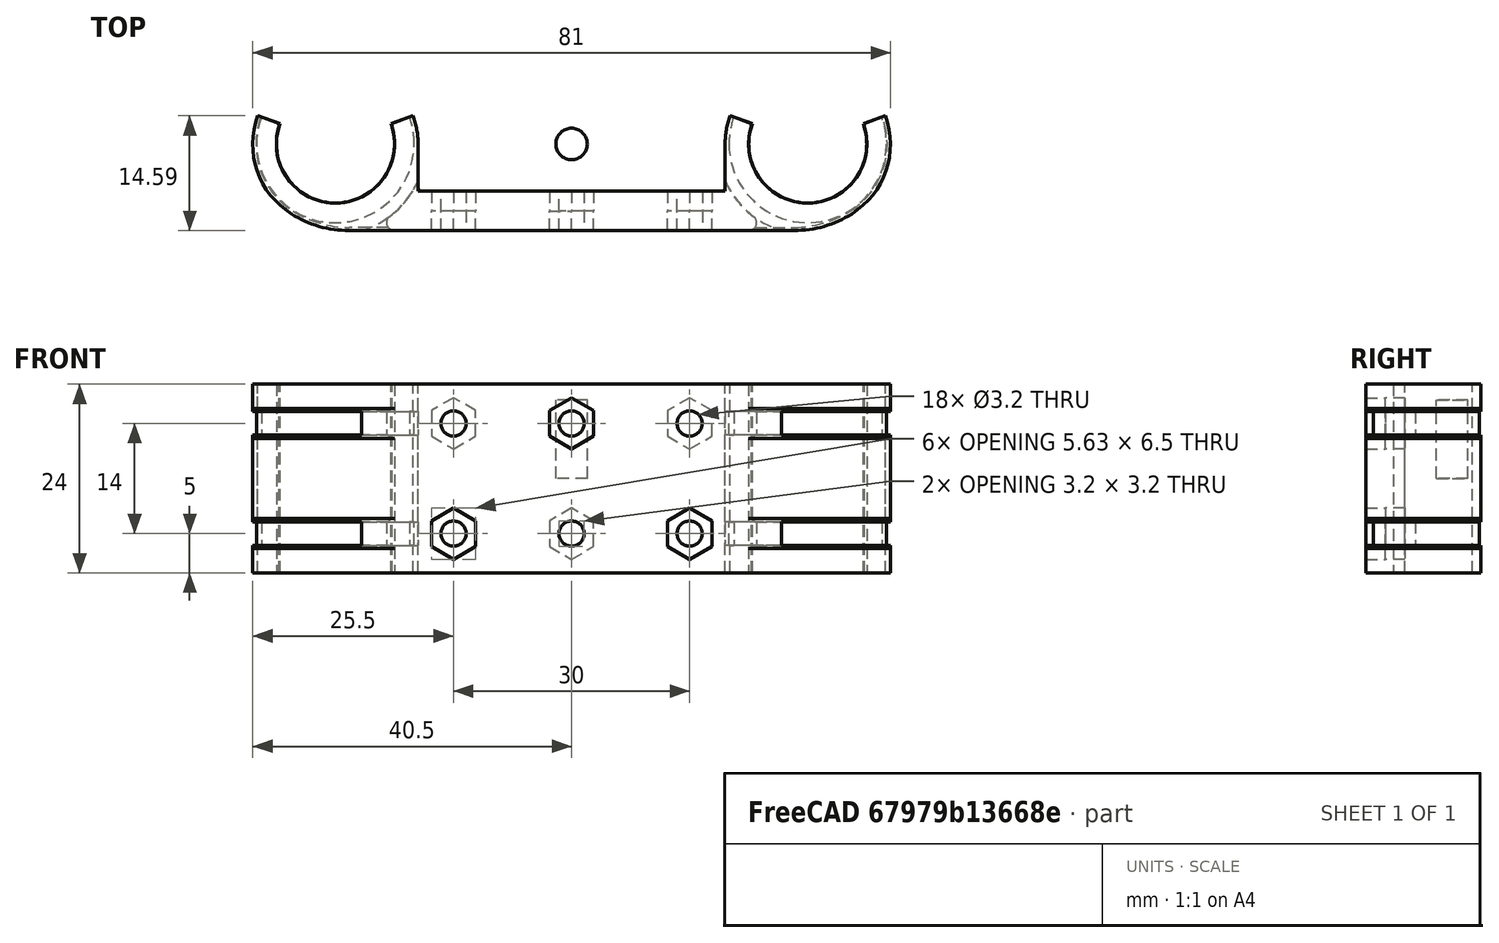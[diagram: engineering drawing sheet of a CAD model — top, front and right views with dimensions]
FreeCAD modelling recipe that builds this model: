
FCSTD DOCUMENT  (FreeCAD 0.16R6712 (Git))
Label: universal_carriage_v1a
License: All rights reserved
LicenseURL: http://en.wikipedia.org/wiki/All_rights_reserved
objects: Spreadsheet::Sheet×5, Mesh::Feature×4, Sketcher::SketchObject×4, PartDesign::Pad×4, Part::FeaturePython×3, Part::MultiFuse×3, Part::Cut×2, Part::Feature×2, PartDesign::Fillet×2, Part::Cylinder×1, App::DocumentObjectGroup×1, Part::Mirroring×1, PartDesign::Chamfer×1
note: 27 computed .brp shape members not serialized (recipe doc carries the construction recipe); baked Part::Feature solids carry a one-line shape summary decoded from their .brp

FEATURE [Mesh::Feature] carriage
FEATURE [Part::Cylinder] Cylinder
  Angle = 360
  Height = 10
  Radius = 2
FEATURE [Mesh::Feature] idler_end_v3
FEATURE [Mesh::Feature] carriage001  label="carriage"
FEATURE [Mesh::Feature] MagCarriage
  Placement = pos=(40,-4,-12) rot=(0.57735,-0.57735,-0.57735;2.0944rad)
FEATURE [Sketcher::SketchObject] Sketch
  sketch-geometry (12):
    g0: ArcOfCircle CenterX=-30 CenterY=0 CenterZ=0 NormalX=0 NormalY=0 NormalZ=1 Radius=7.5 StartAngle=2.79253 EndAngle=6.63225
    g1: ArcOfCircle CenterX=-30 CenterY=0 CenterZ=0 NormalX=0 NormalY=0 NormalZ=1 Radius=10.5 StartAngle=2.79253 EndAngle=4.15082
    g2: LineSegment StartX=-37.0477 StartY=2.56515 StartZ=0 EndX=-39.8668 EndY=3.59121 EndZ=0
    g3: LineSegment StartX=-22.9523 StartY=2.56515 StartZ=0 EndX=-20.1332 EndY=3.59121 EndZ=0
    g4: LineSegment StartX=-19.5 StartY=-6 StartZ=0 EndX=0 EndY=-6 EndZ=0
    g5: LineSegment StartX=0 StartY=-6 StartZ=0 EndX=0 EndY=-11 EndZ=0
    g6: LineSegment [constr] StartX=-37.0477 StartY=2.56515 StartZ=0 EndX=-30 EndY=0 EndZ=0
    g7: LineSegment [constr] StartX=-30 StartY=0 StartZ=0 EndX=-22.9523 EndY=2.56515 EndZ=0
    g8: ArcOfCircle CenterX=-30 CenterY=0 CenterZ=0 NormalX=0 NormalY=0 NormalZ=1 Radius=10.5 StartAngle=0 EndAngle=0.349066
    g9: LineSegment StartX=-19.5 StartY=0 StartZ=0 EndX=-19.5 EndY=-6 EndZ=0
    g10: LineSegment StartX=0 StartY=-11 StartZ=0 EndX=-28.2663 EndY=-11 EndZ=0
    g11: ArcOfCircle CenterX=-28.2663 CenterY=2.75573 CenterZ=0 NormalX=0 NormalY=0 NormalZ=1 Radius=13.7557 StartAngle=4.15082 EndAngle=4.71239
  constraints (35):
    c: PointOnObject(g0,g-1)
    c: DistanceX(g0,g-1) = 30
    c: Coincident(g1,g0)
    c: Radius(g0) = 7.5
    c: Coincident(g2,g0)
    c: Coincident(g1,g2)
    c: Perpendicular(g1,g2)
    c: Coincident(g0,g3)
    c: Horizontal(g4)
    c: Coincident(g4,g5)
    c: Vertical(g5)
    c: Equal(g3,g2)
    c: Coincident(g6,g0)
    c: Coincident(g6,g0)
    c: Angle(g-1,g6) = 2.79253
    c: Coincident(g7,g0)
    c: Coincident(g7,g0)
    c: Angle(g7,g-1) = 2.79253
    c: Coincident(g8,g0)
    c: Coincident(g8,g3)
    c: PointOnObject(g8,g-1)
    c: Coincident(g9,g8)
    c: Coincident(g9,g4)
    c: Vertical(g9)
    c: DistanceY(g4,g-1) = 6
    c: Perpendicular(g0,g3)
    c: Coincident(g5,g10)
    c: Horizontal(g10)
    c: PointOnObject(g4,g-2)
    c: DistanceY(g5,g5) = 5
    c: Coincident(g11,g10)
    c: Coincident(g11,g1)
    c: Tangent(g11,g10)
    c: Tangent(g11,g1)
    c: Distance(g2) = 3
FEATURE [PartDesign::Pad] Pad
  Length = 24
  Length2 = 100
  Midplane = true
  Sketch = -> Sketch
  Type = 0
FEATURE [Spreadsheet::Sheet] Spreadsheet007  label="Screw_M3"
  cells = A1=Name; B1=Value; C1=Description; A2=Designation; B2=M3x10; A3=T; B3(T)==0.1mm + Printer.T; C3=Screw dimension tolerance (including printer T); A4=ideal_r; B4(ideal_r)==1.5mm; C4=Ideal screw thread radius; A5=thread_r; B5(thread_r)==ideal_r + T; C5=Pass through hole radius; A6=thread_length; B6(thread_length)==10mm; C6=Screw thread length; A7=head_r; B7(head_r)==5.7mm / 2 + T; C7=Screw head radius; A8=head_length; B8(head_length)==3mm; C8=Screw head length (height); A9=head_clearance; B9(head_clearance)==10mm; C9=Needed clearance above screw head; A10=head_slope_length; B10(head_slope_length)==ceil((head_r - thread_r) / Printer.default_layer) * Printer.default_layer; C10=45deg slop to make it easier to print; A11=arm_r; B11(arm_r)==head_r + Printer.wall_4d; C11=Holder arm going around head; A12=arm_min_r; B12(arm_min_r)==thread_r + Printer.wall_2d; C12=Holder arm going around thread only; A13=arm_thickness; B13(arm_thickness)==5mm; C13=Suggested arm thickness; A14=cut_r; B14(cut_r)==ideal_r - 0.05mm; C14=Planar threaded hole cut radius; A15=vcut_r; B15(vcut_r)==floor(cut_r / Printer.default_layer) * Printer.default_layer; C15=Vertical threaded hole cut radius
FEATURE [Spreadsheet::Sheet] Spreadsheet005  label="Screw_M6"
  cells = A1=Name; B1=Value; C1=Description; A2=Designation; B2=M6x25; A3=T; B3(T)==0.1mm + Printer.T; C3=Screw dimension tolerance (including printer T); A4=ideal_r; B4(ideal_r)==3mm; C4=Ideal screw thread radius; A5=thread_r; B5(thread_r)==3mm + T; C5=Pass through hole radius; A6=thread_length; B6(thread_length)==25mm; C6=Screw thread length; A7=head_r; B7(head_r)==5mm + T; C7=Screw head radius; A8=head_length; B8(head_length)==4mm; C8=Screw head length (height); A9=arm_r; B9(arm_r)==head_r + Printer.wall_4d; C9=Holder arm going around head; A10=arm_min_r; B10(arm_min_r)==thread_r + Printer.wall_2d; C10=Holder arm going around thread only; A11=arm_thickness; B11(arm_thickness)==7mm; C11=Suggested arm thickness; A12=cut_r; B12(cut_r)==2.9mm; C12=Planar threaded hole cut radius; A13=vcut_r; B13(vcut_r)==floor(cut_r / Printer.default_layer) * Printer.default_layer; C13=Vertical threaded hole cut radius
FEATURE [Spreadsheet::Sheet] Spreadsheet006  label="Nut_M6"
  cells = A1=Name; B1=Value; C1=Description; A2=T; B2(T)==0mm + Printer.T; C2=Dimension tolerance (including printer T); A3=outer_r; B3(outer_r)==11.2mm / 2; C3=Outer most nut radius; A4=width; B4(width)==10mm; C4=Nut side width; A5=thickness; B5(thickness)==5mm; C5=Nut thickness (height); A6=num_of_sides; B6(num_of_sides)=6; C6=Number of sides
FEATURE [Spreadsheet::Sheet] Spreadsheet008  label="Nut_M3"
  cells = A1=Name; B1=Value; C1=Description; A2=T; B2(T)==0mm + Printer.T; C2=Dimension tolerance (including printer T); A3=outer_r; B3(outer_r)==6.5mm / 2 + T; C3=Outer most nut radius; A4=width; B4(width)==5.5mm + T; C4=Nut side width; A5=thickness; B5(thickness)==2.5mm; C5=Nut thickness (height); A6=num_of_sides; B6(num_of_sides)=6; C6=Number of sides
FEATURE [Sketcher::SketchObject] Sketch001
  Placement = pos=(0,-6,0) rot=(1,0,0;1.5708rad)
  expr: Constraints[38] = Nut_M3.outer_r
  sketch-geometry (24):
    g0: LineSegment StartX=-12.1854 StartY=5.375 StartZ=0 EndX=-12.1854 EndY=8.625 EndZ=0
    g1: LineSegment StartX=-12.1854 StartY=8.625 StartZ=0 EndX=-15 EndY=10.25 EndZ=0
    g2: LineSegment StartX=-15 StartY=10.25 StartZ=0 EndX=-17.8146 EndY=8.625 EndZ=0
    g3: LineSegment StartX=-17.8146 StartY=8.625 StartZ=0 EndX=-17.8146 EndY=5.375 EndZ=0
    g4: LineSegment StartX=-17.8146 StartY=5.375 StartZ=0 EndX=-15 EndY=3.75 EndZ=0
    g5: LineSegment StartX=-15 StartY=3.75 StartZ=0 EndX=-12.1854 EndY=5.375 EndZ=0
    g6: Circle [constr] CenterX=-15 CenterY=7 CenterZ=0 NormalX=0 NormalY=0 NormalZ=1 Radius=3.25
    g7: LineSegment StartX=2.81458 StartY=-8.625 StartZ=0 EndX=2.81458 EndY=-5.375 EndZ=0
    g8: LineSegment StartX=2.81458 StartY=-5.375 StartZ=0 EndX=0 EndY=-3.75 EndZ=0
    g9: LineSegment StartX=0 StartY=-3.75 StartZ=0 EndX=-2.81458 EndY=-5.375 EndZ=0
    g10: LineSegment StartX=-2.81458 StartY=-5.375 StartZ=0 EndX=-2.81458 EndY=-8.625 EndZ=0
    g11: LineSegment StartX=-2.81458 StartY=-8.625 StartZ=0 EndX=0 EndY=-10.25 EndZ=0
    g12: LineSegment StartX=0 StartY=-10.25 StartZ=0 EndX=2.81458 EndY=-8.625 EndZ=0
    g13: Circle [constr] CenterX=0 CenterY=-7 CenterZ=0 NormalX=0 NormalY=0 NormalZ=1 Radius=3.25
    g14: LineSegment [constr] StartX=0 StartY=-7 StartZ=0 EndX=0 EndY=0 EndZ=0
    g15: LineSegment [constr] StartX=-15 StartY=7 StartZ=0 EndX=-15 EndY=0 EndZ=0
    g16: LineSegment StartX=17.8146 StartY=5.375 StartZ=0 EndX=17.8146 EndY=8.625 EndZ=0
    g17: LineSegment StartX=17.8146 StartY=8.625 StartZ=0 EndX=15 EndY=10.25 EndZ=0
    g18: LineSegment StartX=15 StartY=10.25 StartZ=0 EndX=12.1854 EndY=8.625 EndZ=0
    g19: LineSegment StartX=12.1854 StartY=8.625 StartZ=0 EndX=12.1854 EndY=5.375 EndZ=0
    g20: LineSegment StartX=12.1854 StartY=5.375 StartZ=0 EndX=15 EndY=3.75 EndZ=0
    g21: LineSegment StartX=15 StartY=3.75 StartZ=0 EndX=17.8146 EndY=5.375 EndZ=0
    g22: Circle [constr] CenterX=15 CenterY=7 CenterZ=0 NormalX=0 NormalY=0 NormalZ=1 Radius=3.25
    g23: LineSegment [constr] StartX=-15 StartY=7 StartZ=0 EndX=15 EndY=7 EndZ=0
  constraints (58):
    c: Coincident(g0,g1)
    c: Coincident(g1,g2)
    c: Coincident(g2,g3)
    c: Coincident(g3,g4)
    c: Coincident(g4,g5)
    c: Coincident(g5,g0)
    c: Equal(g0, g1-g5) x5
    c: PointOnObject(g0,g6)
    c: PointOnObject(g1,g6)
    c: PointOnObject(g2,g6)
    c: PointOnObject(g3,g6)
    c: PointOnObject(g4,g6)
    c: PointOnObject(g5,g6)
    c: Coincident(g7,g8)
    c: Coincident(g8,g9)
    c: Coincident(g9,g10)
    c: Coincident(g10,g11)
    c: Coincident(g11,g12)
    c: Coincident(g12,g7)
    c: Equal(g7, g8-g12) x5
    c: PointOnObject(g7,g13)
    c: PointOnObject(g8,g13)
    c: PointOnObject(g9,g13)
    c: PointOnObject(g10,g13)
    c: PointOnObject(g11,g13)
    c: PointOnObject(g12,g13)
    c: PointOnObject(g13,g-2)
    c: Vertical(g3)
    c: Vertical(g10)
    c: Equal(g6,g13)
    c: Radius(g6) = 3.25
    c: Coincident(g14,g13)
    c: Coincident(g14,g-1)
    c: Coincident(g15,g6)
    c: Vertical(g15)
    c: Equal(g15,g14)
    c: PointOnObject(g15,g-1)
    c: DistanceY(g14,g14) = 7
    c: DistanceX(g15,g-1) = 15
    c: Coincident(g16,g17)
    c: Coincident(g17,g18)
    c: Coincident(g18,g19)
    c: Coincident(g19,g20)
    c: Coincident(g20,g21)
    c: Coincident(g21,g16)
    c: Equal(g16, g17-g21) x5
    c: PointOnObject(g16,g22)
    c: PointOnObject(g17,g22)
    c: PointOnObject(g18,g22)
    c: PointOnObject(g19,g22)
    c: PointOnObject(g20,g22)
    c: PointOnObject(g21,g22)
    c: Coincident(g23,g6)
    c: Coincident(g23,g22)
    c: Horizontal(g23)
    c: Vertical(g19)
    c: Equal(g22,g6)
    c: Symmetric(g22,g6,g-2)
FEATURE [Spreadsheet::Sheet] Spreadsheet011  label="Printer"
  cells = A1=Name; B1=Value; C1=Description; A2=printer; B2=Prusa i3 MK2; C2=Printer name; A3=T; B3(T)==0mm; C3=Dimensional deviation of XY axis; A4=T_v; B4(T_v)==0mm; C4=Dimensional deviation of Z axis; A5=T_max; B5(T_max)==0.4mm; C5=Maximal expected deviation; A6=nozzle_d; B6(nozzle_d)==0.4mm; C6=Nozzle diameter; A7=thinnes_wall; B7(thinnest_wall)==2 * nozzle_d; C7=Thinnest printable wall; A8=wall_2d; B8(wall_2d)==2 * nozzle_d; C8=2D wall without infill; A9=wall_3d; B9(wall_3d)==3 * nozzle_d; C9=3D wall without infill; A10=wall_4d; B10(wall_4d)==4 * nozzle_d; C10=4D wall without infill; A11=wall_5d; B11(wall_5d)==5 * nozzle_d; C11=5D wall without infill; A12=default_layer; B12(default_layer)==0.2mm; C12=Default printing layer height
FEATURE [App::DocumentObjectGroup] Group  label="Documents"
  Group = -> [Spreadsheet007,Spreadsheet005,Spreadsheet006,Spreadsheet008,Spreadsheet011]
FEATURE [PartDesign::Pad] Pad001
  Length = 2.5
  Length2 = 100
  Placement = pos=(0,-6,0) rot=(1,0,0;1.5708rad)
  Sketch = -> Sketch001
  Type = 0
FEATURE [Sketcher::SketchObject] Sketch002
  Placement = pos=(0,-6,0) rot=(1,0,0;1.5708rad)
  expr: Constraints[82] = 1.6mm
  expr: Constraints[38] = Nut_M3.outer_r
  sketch-geometry (30):
    g0: LineSegment [constr] StartX=-12.1854 StartY=5.375 StartZ=0 EndX=-12.1854 EndY=8.625 EndZ=0
    g1: LineSegment [constr] StartX=-12.1854 StartY=8.625 StartZ=0 EndX=-15 EndY=10.25 EndZ=0
    g2: LineSegment [constr] StartX=-15 StartY=10.25 StartZ=0 EndX=-17.8146 EndY=8.625 EndZ=0
    g3: LineSegment [constr] StartX=-17.8146 StartY=8.625 StartZ=0 EndX=-17.8146 EndY=5.375 EndZ=0
    g4: LineSegment [constr] StartX=-17.8146 StartY=5.375 StartZ=0 EndX=-15 EndY=3.75 EndZ=0
    g5: LineSegment [constr] StartX=-15 StartY=3.75 StartZ=0 EndX=-12.1854 EndY=5.375 EndZ=0
    g6: Circle [constr] CenterX=-15 CenterY=7 CenterZ=0 NormalX=0 NormalY=0 NormalZ=1 Radius=3.25
    g7: LineSegment [constr] StartX=2.81458 StartY=-8.625 StartZ=0 EndX=2.81458 EndY=-5.375 EndZ=0
    g8: LineSegment [constr] StartX=2.81458 StartY=-5.375 StartZ=0 EndX=0 EndY=-3.75 EndZ=0
    g9: LineSegment [constr] StartX=0 StartY=-3.75 StartZ=0 EndX=-2.81458 EndY=-5.375 EndZ=0
    g10: LineSegment [constr] StartX=-2.81458 StartY=-5.375 StartZ=0 EndX=-2.81458 EndY=-8.625 EndZ=0
    g11: LineSegment [constr] StartX=-2.81458 StartY=-8.625 StartZ=0 EndX=0 EndY=-10.25 EndZ=0
    g12: LineSegment [constr] StartX=0 StartY=-10.25 StartZ=0 EndX=2.81458 EndY=-8.625 EndZ=0
    g13: Circle [constr] CenterX=0 CenterY=-7 CenterZ=0 NormalX=0 NormalY=0 NormalZ=1 Radius=3.25
    g14: LineSegment [constr] StartX=0 StartY=-7 StartZ=0 EndX=0 EndY=0 EndZ=0
    g15: LineSegment [constr] StartX=-15 StartY=7 StartZ=0 EndX=-15 EndY=0 EndZ=0
    g16: LineSegment [constr] StartX=17.8146 StartY=5.375 StartZ=0 EndX=17.8146 EndY=8.625 EndZ=0
    g17: LineSegment [constr] StartX=17.8146 StartY=8.625 StartZ=0 EndX=15 EndY=10.25 EndZ=0
    g18: LineSegment [constr] StartX=15 StartY=10.25 StartZ=0 EndX=12.1854 EndY=8.625 EndZ=0
    g19: LineSegment [constr] StartX=12.1854 StartY=8.625 StartZ=0 EndX=12.1854 EndY=5.375 EndZ=0
    g20: LineSegment [constr] StartX=12.1854 StartY=5.375 StartZ=0 EndX=15 EndY=3.75 EndZ=0
    g21: LineSegment [constr] StartX=15 StartY=3.75 StartZ=0 EndX=17.8146 EndY=5.375 EndZ=0
    g22: Circle [constr] CenterX=15 CenterY=7 CenterZ=0 NormalX=0 NormalY=0 NormalZ=1 Radius=3.25
    g23: LineSegment [constr] StartX=-15 StartY=7 StartZ=0 EndX=15 EndY=7 EndZ=0
    g24: Circle CenterX=-15 CenterY=7 CenterZ=0 NormalX=0 NormalY=0 NormalZ=1 Radius=1.6
    g25: Circle CenterX=0 CenterY=-7 CenterZ=0 NormalX=0 NormalY=0 NormalZ=1 Radius=1.6
    g26: Circle CenterX=15 CenterY=7 CenterZ=0 NormalX=0 NormalY=0 NormalZ=1 Radius=1.6
    g27: Circle CenterX=-15 CenterY=-7 CenterZ=0 NormalX=0 NormalY=0 NormalZ=1 Radius=1.6
    g28: Circle CenterX=0 CenterY=7 CenterZ=0 NormalX=0 NormalY=0 NormalZ=1 Radius=1.6
    g29: Circle CenterX=15 CenterY=-7 CenterZ=0 NormalX=0 NormalY=0 NormalZ=1 Radius=1.6
  constraints (71):
    c: Coincident(g0,g1)
    c: Coincident(g1,g2)
    c: Coincident(g2,g3)
    c: Coincident(g3,g4)
    c: Coincident(g4,g5)
    c: Coincident(g5,g0)
    c: Equal(g0, g1-g5) x5
    c: PointOnObject(g0,g6)
    c: PointOnObject(g1,g6)
    c: PointOnObject(g2,g6)
    c: PointOnObject(g3,g6)
    c: PointOnObject(g4,g6)
    c: PointOnObject(g5,g6)
    c: Coincident(g7,g8)
    c: Coincident(g8,g9)
    c: Coincident(g9,g10)
    c: Coincident(g10,g11)
    c: Coincident(g11,g12)
    c: Coincident(g12,g7)
    c: Equal(g7, g8-g12) x5
    c: PointOnObject(g7,g13)
    c: PointOnObject(g8,g13)
    c: PointOnObject(g9,g13)
    c: PointOnObject(g10,g13)
    c: PointOnObject(g11,g13)
    c: PointOnObject(g12,g13)
    c: PointOnObject(g13,g-2)
    c: Vertical(g3)
    c: Vertical(g10)
    c: Equal(g6,g13)
    c: Radius(g6) = 3.25
    c: Coincident(g14,g13)
    c: Coincident(g14,g-1)
    c: Coincident(g15,g6)
    c: Vertical(g15)
    c: Equal(g15,g14)
    c: PointOnObject(g15,g-1)
    c: DistanceY(g14,g14) = 7
    c: DistanceX(g15,g-1) = 15
    c: Coincident(g16,g17)
    c: Coincident(g17,g18)
    c: Coincident(g18,g19)
    c: Coincident(g19,g20)
    c: Coincident(g20,g21)
    c: Coincident(g21,g16)
    c: Equal(g16, g17-g21) x5
    c: PointOnObject(g16,g22)
    c: PointOnObject(g17,g22)
    c: PointOnObject(g18,g22)
    c: PointOnObject(g19,g22)
    c: PointOnObject(g20,g22)
    c: PointOnObject(g21,g22)
    c: Coincident(g23,g6)
    c: Coincident(g23,g22)
    c: Horizontal(g23)
    c: Vertical(g19)
    c: Equal(g22,g6)
    c: Symmetric(g22,g6,g-2)
    c: Coincident(g24,g6)
    c: Coincident(g25,g13)
    c: Coincident(g26,g22)
    c: PointOnObject(g28,g23)
    c: Symmetric(g6,g27,g-1)
    c: Symmetric(g28,g13,g-1)
    c: Symmetric(g22,g29,g-1)
    c: Equal(g29,g25)
    c: Equal(g25,g27)
    c: Equal(g27,g24)
    c: Equal(g24,g28)
    c: Equal(g28,g26)
    c: Radius(g27) = 1.6
FEATURE [PartDesign::Pad] Pad002
  Length = 10
  Length2 = 100
  Placement = pos=(0,-6,0) rot=(1,0,0;1.5708rad)
  Sketch = -> Sketch002
  Type = 0
FEATURE [Part::FeaturePython] Clone  label="Clone of Pad001"  # Draft clone (typed FeaturePython)
  Objects = -> [Pad001]
  Placement = pos=(0,-11,0) rot=(-1,0,0;1.5708rad)
  Scale = (1,1,1)
FEATURE [Part::MultiFuse] Fusion
  Shapes = -> [Clone,Pad002,Pad001]
FEATURE [Sketcher::SketchObject] Sketch003
  sketch-geometry (2):
    g0: Circle CenterX=-30 CenterY=0 CenterZ=0 NormalX=0 NormalY=0 NormalZ=1 Radius=10
    g1: Circle CenterX=-30 CenterY=0 CenterZ=0 NormalX=0 NormalY=0 NormalZ=1 Radius=11.5
  constraints (5):
    c: PointOnObject(g0,g-1)
    c: Coincident(g1,g0)
    c: DistanceX(g0,g-1) = 30
    c: Radius(g0) = 10
    c: Radius(g1) = 11.5
FEATURE [PartDesign::Pad] Pad003
  Length = 3
  Length2 = 100
  Midplane = true
  Sketch = -> Sketch003
  Type = 0
FEATURE [Part::FeaturePython] Clone001  label="Clone of Pad003"  # Draft clone (typed FeaturePython)
  Objects = -> [Pad003]
  Placement = pos=(0,0,7) rot=(0,0,1;0rad)
  Scale = (1,1,1)
FEATURE [Part::FeaturePython] Clone002  label="Clone of Pad003"  # Draft clone (typed FeaturePython)
  Objects = -> [Pad003]
  Placement = pos=(0,0,-7) rot=(0,0,1;0rad)
  Scale = (1,1,1)
FEATURE [Part::MultiFuse] Fusion002
  Shapes = -> [Clone001,Clone002]
FEATURE [Part::Cut] Cut
  Base = -> Pad
  Tool = -> Fusion002
FEATURE [Part::Mirroring] Part__Mirroring  label="Cut (Mirror #1)"
  Base = (0,0,0)
  Normal = (1,0,0)
  Source = -> Cut
FEATURE [Part::MultiFuse] Fusion003
  Shapes = -> [Part__Mirroring,Cut]
FEATURE [Part::Cut] Cut001
  Base = -> Fusion003
  Tool = -> Fusion
FEATURE [Part::Feature] Cut001001  label="Cut001"
  shape: bbox 81 x 14.59 x 24 mm, 94 faces (baked)
FEATURE [PartDesign::Chamfer] Chamfer
  Base = -> Cut001001 [Edge129,Edge156,Edge146,Edge104,Edge49,Edge34,Edge30,Edge15]
  Size = 0.4
FEATURE [PartDesign::Fillet] Fillet
  Base = -> Chamfer [Edge186,Edge177,Edge165,Edge154,Edge5,Edge44]
  Radius = 0.5
FEATURE [PartDesign::Fillet] Fillet001
  Base = -> Fillet [Edge133,Edge128,Edge116,Edge121]
  Radius = 1
FEATURE [Part::Feature] Fillet001001  label="universal_carriage-v1"
  shape: bbox 81 x 14.59 x 24 mm, 128 faces (baked)
